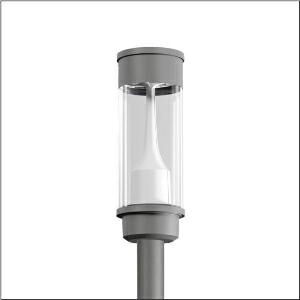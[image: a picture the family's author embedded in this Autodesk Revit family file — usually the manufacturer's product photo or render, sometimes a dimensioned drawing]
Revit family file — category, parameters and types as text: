
# Revit family: litepole_iq___pl1_2s_5xa5415jf14h000022_dba0
name_source: partatom
category: Lighting Fixtures
units: mm (PartAtom-declared; Revit-internal decimal feet)

## family parameters
Cut with Voids When Loaded = No
Host = Face
Light Source = No
Part Type = Normal
Room Calculation Point = No
Round Connector Dimension = Use Diameter
Shared = No

## types (1)
- --- (1 x LED, 2970 lm, 19.3 W, 3000K)
    Apparent Load = 19 VA
    CIE Flux Codes = 23 62 94 96 100
    Color Rendering = 70
    Color Temperature = 3000K
    Default Elevation = 1800 mm
    Description = Litepole iQ, mast luminaire, Module 540 iQ-SR, primary light control with 3 zone facetted reflector, of plastic, silver coated, highly specular, structured, primary optical cover: cover, of PMMA, transparent, light distribution: PL1.2s, light emission: direct distribution, primary light characteristic: symmetric, installation type: post-top, LED, High Power LED, rated luminous flux: 2.970lm, luminous efficacy: 154lm/W, light colour: 730, colour temperature: 3000K, control gear: ECG iQ, control: Street-Remote, Auto-Match, Temp-Guard, Lumen-Switch, Night-Set, Smart-Wire, Light-Fading, Desk-Remote (wireless, voltage-free reading and setting of iQ features in the workshop via application-optimized NFC function/RFID function), optimised constant luminous flux control (CLO 2.0), pre-setting: logarithmic dimming characteristic, mains connection: 230..240V, AC, 50/60Hz, connection cable pre-assembled, cable length: 5,5m, wiring characteristics: H07RN-F, start of lifetime: 19W, end of service life: 21W, reduction: 10W, luminaire housing, upper part, of glass-fibre reinforced polyester, coated, Siteco® metallic grey (DB 702S), diameter: 210mm, height: 590mm, spigot size: d x l = 76 x 70mm (post-top) | with reducer (optional accessory) 60 x 70mm, post-top mast mounting element, of diecast aluminium, coated, Siteco® metallic grey (DB 702S), Module 540 iQ-SR, traffic white (RAL 9016), equipment: standard, protection rating (complete): IP65, insulation class (complete): insulation class II (safety insulation), certification: CE, ENEC, VDE, packaging unit: 1 piece

Light Distribution: PL1.2s
    Height = 590 mm
    Lamp = 1 x LED
    Lamp Light Flux = 2970 lm
    Lamp Power = 19.3 W
    Lamp count = 1
    Length = 220 mm
    Luminous efficacy = 154 lm/W
    Manufacturer = Siteco
    ModVariant = No
    Model = 5XA5415JF14H000022
    Number of Poles = 1
    OnlyDefault = Yes
    Power Factor = 1
    Product Name = Litepole iQ | PL1.2s
    Product group = mast luminaire | pylon top
    ProductGroupID = 6100
    Protection Class = Protection class II
    Protection Degree = IP 65
    RLX_Detail_Level = 1
    RLX_Emergency_Light_Flux = 0 lm
    RLX_Emergency_Type = 0
    RLX_Emergency_Type_DB = No
    RlxData = <blob elided: 40497 chars, md5=6ee38081>
    Socket = socket
    Standby Power = 0 W
    System Light Flux = 2970 lm
    System Power = 19 W
    Type Comments = factory setting: luminous flux: 100 % | dim-lin: 254 | 403 mA
    Type Image = l_1006025.jpg
    URL = http://relux.com
    VarID = @adj_114685
    Voltage = 0 V
    Weight = 0.00 kg
    Width = 0 mm  [stored 0 ft]

note: [stored X ft] marks values corroborated as IEEE doubles in the binary element streams (Revit-internal decimal feet)

## geometry (parser evidence)
native form markers: Blend x4, Sweep x9
no freeform markers — native parametric forms only
